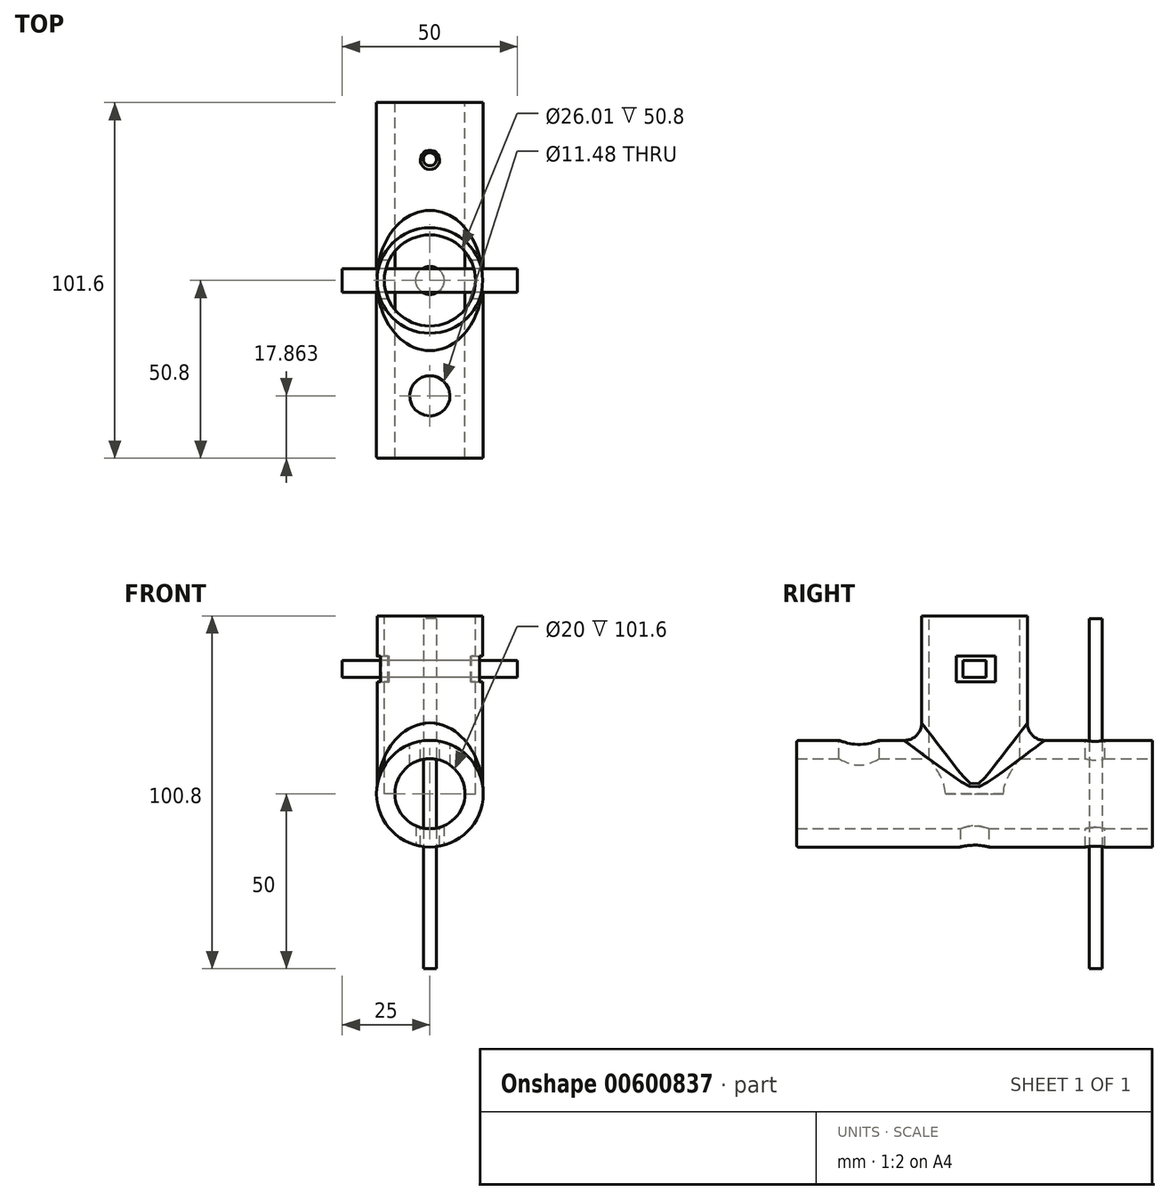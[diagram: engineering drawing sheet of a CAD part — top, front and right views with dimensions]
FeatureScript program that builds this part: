
annotation { "Feature Type Name" : "Feature", "Feature Type Description" : "" }
export const myFeature = defineFeature(function(context is Context, id is Id, definition is map)
    precondition{}
    {
        {
            var Q0;
            Q0=qCreatedBy(makeId("Front.planeOp"),FACE);
            var sketch = newSketch(context, id + "F0", { "sketchPlane" : qUnion([Q0])});
            skCircle(sketch, "E0", {"center": v(0, 0) * mm, "radius": 15.22 * mm});
            skCircle(sketch, "E1", {"center": v(0, 0) * mm, "radius": 10 * mm});
            skSolve(sketch);
        }
        {
            var Q0;
            Q0=makeQuery(id+"F0.imprint","IMPRINT",FACE,{"disambiguationData":[TD([[makeQuery(id+"F0.imprint","IMPRINT",EDGE,{"derivedFrom":sQuery(id+"F0.wireOp",EDGE,"E0")}),1.0]])]});
            extrude(context, id + "F1", {"entities" : qUnion([Q0]), "endBound" : BoundingType.SYMMETRIC, "depth" : 101.6 * mm, "offsetDistance" : 25.4 * mm});
        }
        {
            var Q0;
            Q0=qCreatedBy(makeId("Top.planeOp"),FACE);
            var sketch = newSketch(context, id + "F2", { "sketchPlane" : qUnion([Q0])});
            skCircle(sketch, "E2", {"center": v(0, 0) * mm, "radius": 15.08 * mm});
            skSolve(sketch);
        }
        {
            var Q0;
            Q0 = qSketchRegion(id + "F2", true);
            extrude(context, id + "F3", {"entities" : qUnion([Q0]), "operationType" : NewBodyOperationType.ADD, "depth" : 50.8 * mm, "offsetDistance" : 25.4 * mm});
        }
        {
            var Q0;
            Q0=makeQuery(id+"F3.opExtrude","CAP_FACE",FACE,{"disambiguationData":[OSD([sQuery(id+"F2.wireOp",EDGE,"E2")])],"isStart":false});
            var sketch = newSketch(context, id + "F4", { "sketchPlane" : qUnion([Q0])});
            skCircle(sketch, "E3", {"center": v(0, 0) * mm, "radius": 13 * mm});
            skSolve(sketch);
        }
        {
            var Q0;
            Q0=makeQuery(id+"F4.imprint","IMPRINT",FACE,{"disambiguationData":[TD([[makeQuery(id+"F4.imprint","IMPRINT",EDGE,{"derivedFrom":sQuery(id+"F4.wireOp",EDGE,"E3")}),1.0]])]});
            extrude(context, id + "F5", {"entities" : qUnion([Q0]), "operationType" : NewBodyOperationType.REMOVE, "oppositeDirection" : true, "depth" : 50.8 * mm, "offsetDistance" : 25.4 * mm});
        }
        {
            var Q0;
            Q0=qCreatedBy(makeId("Right.planeOp"),FACE);
            cPlane(context, id + "F6", {"entities" : qUnion([Q0]), "cplaneType" : CPlaneType.OFFSET, "offset" : 30.16 * mm / 2, "width" : 150 * mm, "height" : 150 * mm});
        }
        {
            var Q0;
            Q0=qCreatedBy(id+"F6.planeOp",FACE);
            var sketch = newSketch(context, id + "F7", { "sketchPlane" : qUnion([Q0])});
            skLineSegment(sketch, "E4.bottom", {"start": v(-5.14, 39.31) * mm, "end": v(5.92, 39.31) * mm});
            skLineSegment(sketch, "E4.top", {"start": v(-5.14, 31.94) * mm, "end": v(5.92, 31.94) * mm});
            skLineSegment(sketch, "E4.left", {"start": v(-5.14, 39.31) * mm, "end": v(-5.14, 31.94) * mm});
            skLineSegment(sketch, "E4.right", {"start": v(5.92, 39.31) * mm, "end": v(5.92, 31.94) * mm});
            skSolve(sketch);
        }
        {
            var Q0;
            Q0 = qSketchRegion(id + "F7", true);
            extrude(context, id + "F8", {"entities" : qUnion([Q0]), "operationType" : NewBodyOperationType.REMOVE, "oppositeDirection" : true, "depth" : 43.2 * mm, "offsetDistance" : 25 * mm});
        }
        {
            var Q0;
            Q0=qCreatedBy(makeId("Front.planeOp"),FACE);
            cPlane(context, id + "F9", {"entities" : qUnion([Q0]), "cplaneType" : CPlaneType.OFFSET, "offset" : (101.6 / 2) * mm, "width" : 150 * mm, "height" : 150 * mm});
        }
        {
            var Q0;
            Q0=qCreatedBy(id+"F9.planeOp",FACE);
            var sketch = newSketch(context, id + "F10", { "sketchPlane" : qUnion([Q0])});
            skCircle(sketch, "E5", {"center": v(0, 0) * mm, "radius": 10 * mm});
            skSolve(sketch);
        }
        {
            var Q0;
            Q0 = qSketchRegion(id + "F10", true);
            extrude(context, id + "F11", {"entities" : qUnion([Q0]), "operationType" : NewBodyOperationType.REMOVE, "oppositeDirection" : true, "depth" : 135.8 * mm, "offsetDistance" : 25 * mm});
        }
        {
            var Q0;
            Q0=makeQuery(id+"F3.boolean.opBoolean","INTERSECT",EDGE,{"derivedFrom":[makeQuery(id+"F1.opExtrude","SWEPT_FACE",FACE,{"disambiguationData":[OSD([sQuery(id+"F0.wireOp",EDGE,"E0")])]}),makeQuery(id+"F3.opExtrude","SWEPT_FACE",FACE,{"disambiguationData":[OSD([sQuery(id+"F2.wireOp",EDGE,"E2")])]})]});
            fillet(context, id + "F12", {"entities" : qUnion([Q0]), "radius" : 5 * mm, "tangentPropagation" : true, "allowEdgeOverflow" : false});
        }
        {
            var Q0;
            Q0=makeQuery(id+"F1.opExtrude","CAP_EDGE",EDGE,{"disambiguationData":[OSD([sQuery(id+"F0.wireOp",EDGE,"E0")])],"isStart":false});
            fillet(context, id + "F13", {"entities" : qUnion([Q0]), "radius" : 0.5 * mm, "tangentPropagation" : true, "allowEdgeOverflow" : false});
        }
        {
            var Q0;
            Q0=qCreatedBy(makeId("Right.planeOp"),FACE);
            var sketch = newSketch(context, id + "F14", { "sketchPlane" : qUnion([Q0])});
            skLineSegment(sketch, "E6.bottom", {"start": v(3.36, 38.01) * mm, "end": v(-3.36, 38.01) * mm});
            skLineSegment(sketch, "E6.top", {"start": v(3.36, 33.3) * mm, "end": v(-3.36, 33.3) * mm});
            skLineSegment(sketch, "E6.left", {"start": v(3.36, 38.01) * mm, "end": v(3.36, 33.3) * mm});
            skLineSegment(sketch, "E6.right", {"start": v(-3.36, 38.01) * mm, "end": v(-3.36, 33.3) * mm});
            skPoint(sketch, "E6.middle", {"position": v(0, 35.66) * mm});
            skSolve(sketch);
        }
        {
            var Q0;
            Q0=makeQuery(id+"F14.imprint","IMPRINT",FACE,{"disambiguationData":[TD([[makeQuery(id+"F14.imprint","IMPRINT",EDGE,{"derivedFrom":sQuery(id+"F14.wireOp",EDGE,"E6.bottom")}),1.0]])]});
            extrude(context, id + "F15", {"entities" : qUnion([Q0]), "endBound" : BoundingType.SYMMETRIC, "depth" : 50 * mm, "offsetDistance" : 25 * mm});
        }
        {
            var Q0;
            Q0=qCreatedBy(makeId("Top.planeOp"),FACE);
            cPlane(context, id + "F16", {"entities" : qUnion([Q0]), "cplaneType" : CPlaneType.OFFSET, "offset" : 25 * mm, "oppositeDirection" : true, "width" : 150 * mm, "height" : 150 * mm});
        }
        {
            var Q0;
            Q0=qCreatedBy(id+"F16.planeOp",FACE);
            var sketch = newSketch(context, id + "F17", { "sketchPlane" : qUnion([Q0])});
            skCircle(sketch, "E7", {"center": v(0, 0) * mm, "radius": 4.02 * mm});
            skSolve(sketch);
        }
        {
            var Q0;
            Q0=makeQuery(id+"F17.imprint","IMPRINT",FACE,{"disambiguationData":[TD([[makeQuery(id+"F17.imprint","IMPRINT",EDGE,{"derivedFrom":sQuery(id+"F17.wireOp",EDGE,"E7")}),1.0]])]});
            extrude(context, id + "F18", {"entities" : qUnion([Q0]), "operationType" : NewBodyOperationType.REMOVE, "depth" : 25 * mm, "offsetDistance" : 25 * mm});
        }
        {
            var Q0;
            Q0=qCreatedBy(makeId("Top.planeOp"),FACE);
            cPlane(context, id + "F19", {"entities" : qUnion([Q0]), "cplaneType" : CPlaneType.OFFSET, "offset" : 20 * mm, "width" : 150 * mm, "height" : 150 * mm});
        }
        {
            var Q0;
            Q0=qCreatedBy(id+"F19.planeOp",FACE);
            var sketch = newSketch(context, id + "F20", { "sketchPlane" : qUnion([Q0])});
            skCircle(sketch, "E8", {"center": v(0, -32.94) * mm, "radius": 5.74 * mm});
            skSolve(sketch);
        }
        {
            var Q0;
            Q0=makeQuery(id+"F20.imprint","IMPRINT",FACE,{"disambiguationData":[TD([[makeQuery(id+"F20.imprint","IMPRINT",EDGE,{"derivedFrom":sQuery(id+"F20.wireOp",EDGE,"E8")}),1.0]])]});
            extrude(context, id + "F21", {"entities" : qUnion([Q0]), "operationType" : NewBodyOperationType.REMOVE, "oppositeDirection" : true, "depth" : 25 * mm, "offsetDistance" : 25 * mm});
        }
        {
            var Q0;
            Q0=qCreatedBy(id+"F19.planeOp",FACE);
            var sketch = newSketch(context, id + "F22", { "sketchPlane" : qUnion([Q0])});
            skPoint(sketch, "E9", {"position": v(0, 34.43) * mm});
            skSolve(sketch);
        }
        {
            var Q0;
            Q0=sQuery(id+"F22.wireOp",VERTEX,"E9");
            var Q1;
            Q1=makeQuery(id+"F1.opExtrude","SWEPT_BODY",BODY,{"disambiguationData":[OSD([sQuery(id+"F0.wireOp",EDGE,"E0"),sQuery(id+"F0.wireOp",EDGE,"E1")])]});
            hole(context, id + "F23", {"style" : HoleStyle.SIMPLE, "endStyle" : HoleEndStyle.THROUGH, "standardTappedOrClearance" : lookupTablePath({ "standard" : "ISO", "fit" : "Normal", "size" : "M5", "type" : "Clearance" }), "standardBlindInLast" : lookupTablePath({ "fit" : "Standard", "standard" : "ISO", "size" : "M5", "type" : "Clearance" }), "holeDiameter" : 5.5 * mm, "majorDiameter" : 5 * mm, "isTappedThrough" : true, "tappedDepth" : 2.6 * mm, "tapClearance" : 3, "startFromSketch" : true, "locations" : qUnion([Q0]), "scope" : qUnion([Q1])});
        }
        {
            var Q0;
            Q0=qCreatedBy(makeId("Top.planeOp"),FACE);
            var sketch = newSketch(context, id + "F24", { "sketchPlane" : qUnion([Q0])});
            skCircle(sketch, "E10", {"center": v(0, 34.62) * mm, "radius": 1.86 * mm});
            skSolve(sketch);
        }
        {
            var Q0;
            Q0=makeQuery(id+"F24.imprint","IMPRINT",FACE,{"disambiguationData":[TD([[makeQuery(id+"F24.imprint","IMPRINT",EDGE,{"derivedFrom":sQuery(id+"F24.wireOp",EDGE,"E10")}),1.0]])]});
            extrude(context, id + "F25", {"entities" : qUnion([Q0]), "endBound" : BoundingType.SYMMETRIC, "depth" : 100 * mm, "offsetDistance" : 25 * mm});
        }
    });
